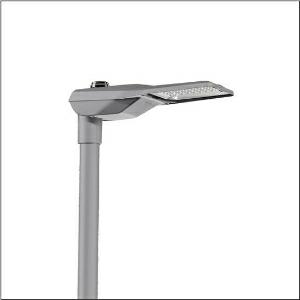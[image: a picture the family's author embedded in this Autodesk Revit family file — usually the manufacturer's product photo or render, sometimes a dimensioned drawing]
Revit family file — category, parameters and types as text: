
# Revit family: streetlight_sl_21_mini___pl52_5xe6h47n08gb_a206
name_source: partatom
category: Lighting Fixtures
units: mm (PartAtom-declared; Revit-internal decimal feet)

## family parameters
Cut with Voids When Loaded = No
Host = Face
Light Source = No
Part Type = Normal
Room Calculation Point = No
Round Connector Dimension = Use Diameter
Shared = No

## types (1)
- --- (1 x LED, 6080 lm, 40.4 W, 4000K)
    Apparent Load = 40 VA
    CIE Flux Codes = 27 59 98 100 100
    Color Rendering = 70
    Color Temperature = 4000K
    Default Elevation = 1800 mm
    Description = Streetlight SL 21 mini, mast luminaire, primary light control with lens, of PMMA, primary optical cover: cover, of toughened safety glass, transparent, light distribution: PL52, light emission: direct distribution, primary light characteristic: asymmetric, installation type: side-entry, LED, 3G 1.5mm², High Power LED, rated luminous flux: 6.080lm, luminous efficacy: 151lm/W, light colour: 740, colour temperature: 4000K, control gear: NEMA (7pin), control: overheat protection, pre-setting: linear dimming characteristic, constant luminous flux control, time-dependent luminous flux control, flexible luminous flux parameterisation, mains connection: 230..240V, AC, 50/60Hz, connection cable pre-assembled, cable length: 8,5m, wiring characteristics: H07RN-F, start of lifetime: 40W, end of service life: 41W, reduction: 19W, luminaire housing, of diecast aluminium (EN AC-44300), powder-coated, Siteco® metallic grey (DB 702S), corrosivity category C5 mid according to DIN EN ISO 12944, multi-level sealing system, sealing non-destructively replaceable, inclination adjustable: 0°, 5°, 10°, 15°, length: 628mm, width: 235mm, height: 110mm, spigot size: 42mm (side-entry), mounting height: 4..8m, protection rating (complete): IP66, insulation class (complete): insulation class I (protective earthing), certification: CE, ENEC, ENEC+, VDE, impact resistance: IK10, permissible operating ambient temperature for outdoor applications: -40..+50°C, standard-compliant lighting for roads and squares, packaging unit: 1 piece

Light Distribution: PL52
    Height = 110 mm
    Lamp = 1 x LED
    Lamp Light Flux = 6080 lm
    Lamp Power = 40.4 W
    Lamp count = 1
    Length = 625 mm
    Luminous efficacy = 151 lm/W
    Manufacturer = Siteco
    ModVariant = No
    Model = 5XE6H47N08GB
    Number of Poles = 1
    OnlyDefault = Yes
    Power Factor = 1
    Product Name = Streetlight SL 21 mini | PL52
    Product group = mast luminaire | pylon top
    ProductGroupID = 6100
    Protection Class = Protection class I
    Protection Degree = IP 66
    RLX_Detail_Level = 1
    RLX_Emergency_Light_Flux = 0 lm
    RLX_Emergency_Type = 0
    RLX_Emergency_Type_DB = No
    RlxData = <blob elided: 35425 chars, md5=12c810a3>
    Socket = socket
    Standby Power = 0 W
    System Light Flux = 6080 lm
    System Power = 40 W
    Type Comments = factory setting: luminous flux: 100 % | dim-lin: 254 | 812 mA
    Type Image = l_1294379.jpg
    URL = http://relux.com
    VarID = @adj_137006
    Voltage = 0 V
    Weight = 0.00 kg
    Width = 234 mm

## geometry (parser evidence)
native form markers: Blend x4, Sweep x11
no freeform markers — native parametric forms only
